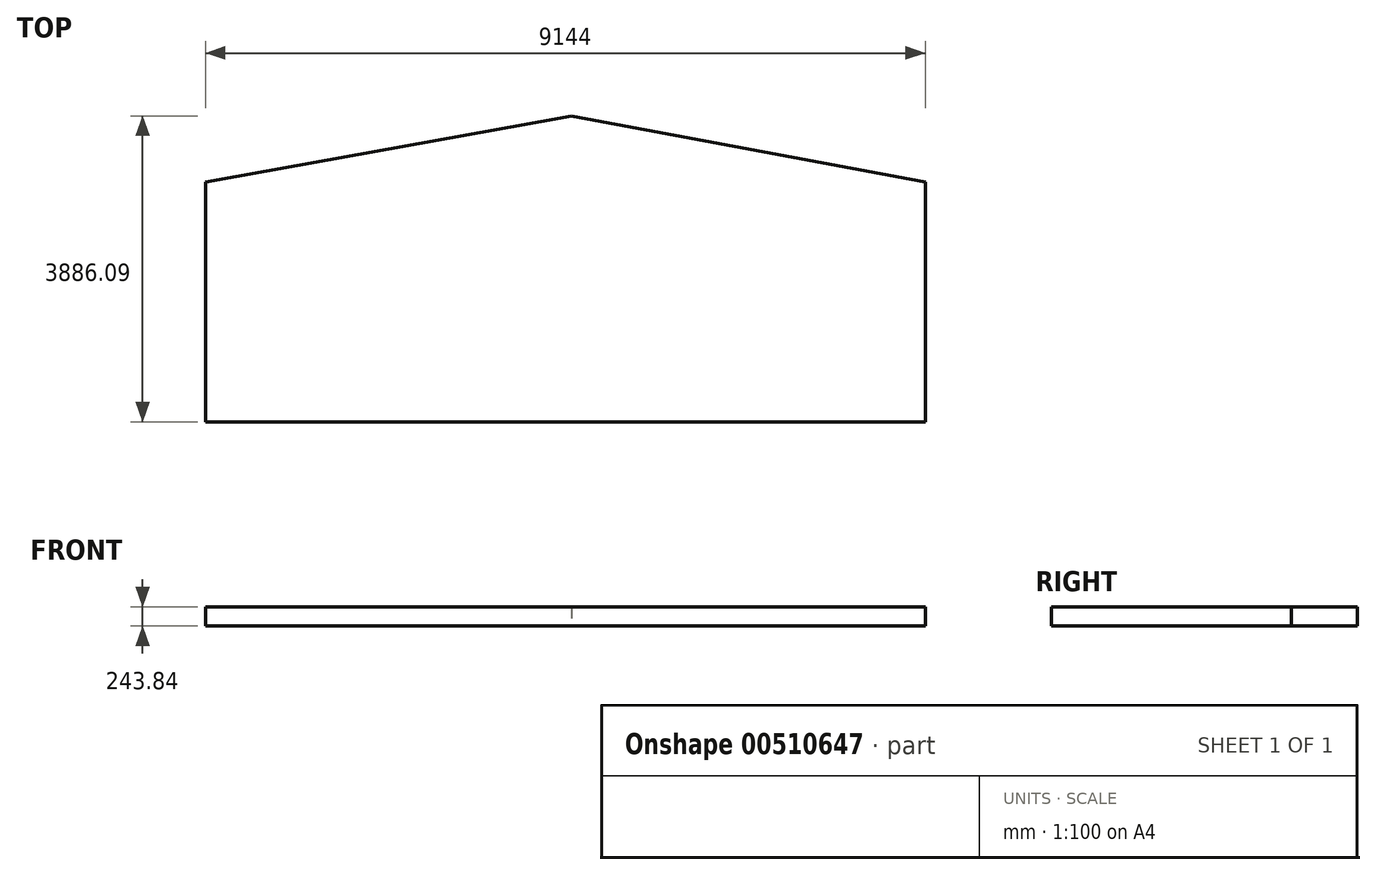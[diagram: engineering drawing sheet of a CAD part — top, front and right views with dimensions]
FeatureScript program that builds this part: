
annotation { "Feature Type Name" : "Feature", "Feature Type Description" : "" }
export const myFeature = defineFeature(function(context is Context, id is Id, definition is map)
    precondition{}
    {
        {
            var Q0;
            Q0=qCreatedBy(makeId("Top.planeOp"),FACE);
            var sketch = newSketch(context, id + "F0", { "sketchPlane" : qUnion([Q0])});
            skLineSegment(sketch, "E0", {"start": v(-4585.24, 2005.76) * mm, "end": v(-4585.24, -1042.24) * mm});
            skLineSegment(sketch, "E1", {"start": v(-4585.24, -1042.24) * mm, "end": v(4558.76, -1042.24) * mm});
            skLineSegment(sketch, "E2", {"start": v(4558.76, -1042.24) * mm, "end": v(4558.76, 2005.76) * mm});
            skLineSegment(sketch, "E3", {"start": v(4558.76, 2005.76) * mm, "end": v(64.23, 2843.85) * mm});
            skLineSegment(sketch, "E4", {"start": v(64.23, 2843.85) * mm, "end": v(-4585.24, 2005.76) * mm});
            skSolve(sketch);
        }
        {
            var Q0;
            Q0 = qSketchRegion(id + "F0", true);
            extrude(context, id + "F1", {"entities" : qUnion([Q0]), "depth" : 243.84 * mm, "offsetDistance" : 30.48 * mm});
        }
    });
